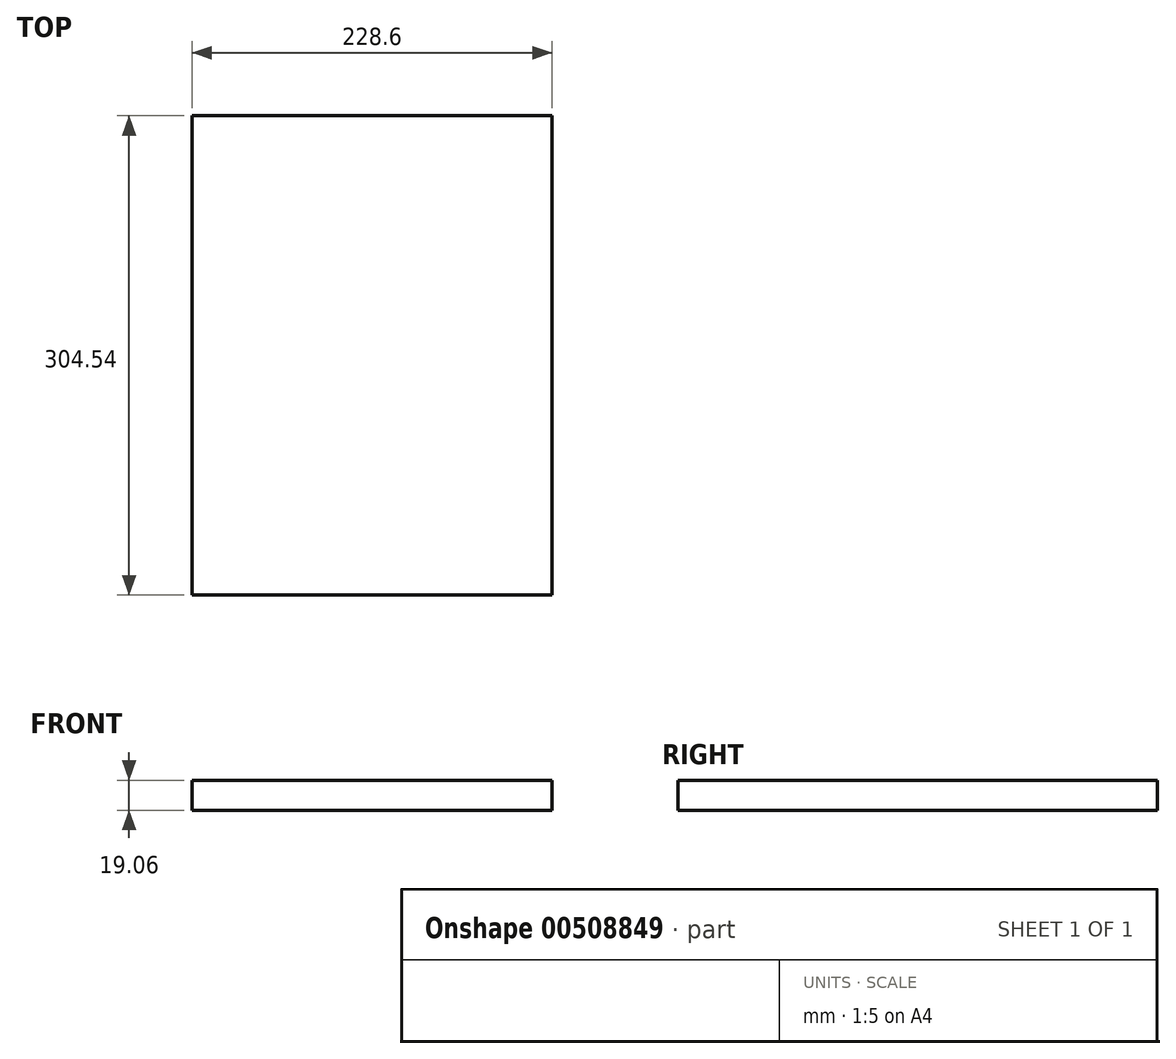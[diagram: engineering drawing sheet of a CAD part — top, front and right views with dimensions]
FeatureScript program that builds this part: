
annotation { "Feature Type Name" : "Feature", "Feature Type Description" : "" }
export const myFeature = defineFeature(function(context is Context, id is Id, definition is map)
    precondition{}
    {
        {
            var Q0;
            Q0=qCreatedBy(makeId("Top.planeOp"),FACE);
            var sketch = newSketch(context, id + "F0", { "sketchPlane" : qUnion([Q0])});
            skLineSegment(sketch, "E0.bottom", {"start": v(114.3, -152.27) * mm, "end": v(-114.3, -152.27) * mm});
            skLineSegment(sketch, "E0.top", {"start": v(114.3, 152.27) * mm, "end": v(-114.3, 152.27) * mm});
            skLineSegment(sketch, "E0.left", {"start": v(114.3, -152.27) * mm, "end": v(114.3, 152.27) * mm});
            skLineSegment(sketch, "E0.right", {"start": v(-114.3, -152.27) * mm, "end": v(-114.3, 152.27) * mm});
            skPoint(sketch, "E0.middle", {"position": v(0, 0) * mm});
            skSolve(sketch);
        }
        {
            var Q0;
            Q0=makeQuery(id+"F0.imprint","IMPRINT",FACE,{"disambiguationData":[TD([[makeQuery(id+"F0.imprint","IMPRINT",EDGE,{"derivedFrom":sQuery(id+"F0.wireOp",EDGE,"E0.bottom")}),-1.0]])]});
            extrude(context, id + "F1", {"entities" : qUnion([Q0]), "endBound" : BoundingType.SYMMETRIC, "depth" : 19.05 * mm});
        }
    });
